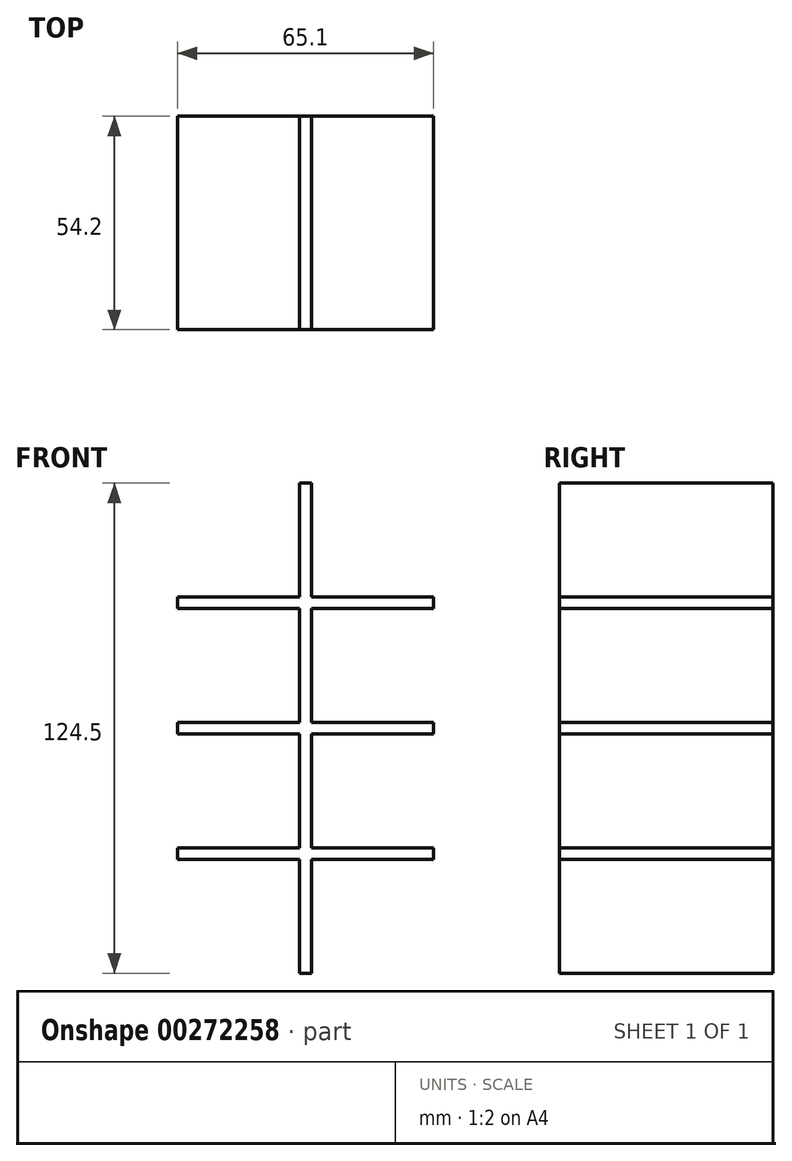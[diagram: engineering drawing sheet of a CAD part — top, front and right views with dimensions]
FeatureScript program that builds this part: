
annotation { "Feature Type Name" : "Feature", "Feature Type Description" : "" }
export const myFeature = defineFeature(function(context is Context, id is Id, definition is map)
    precondition{}
    {
        {
            var Q0;
            Q0=qCreatedBy(makeId("Front.planeOp"),FACE);
            var sketch = newSketch(context, id + "F0", { "sketchPlane" : qUnion([Q0])});
            skLineSegment(sketch, "E0", {"start": v(1.5, 30.37) * mm, "end": v(1.5, 1.5) * mm});
            skLineSegment(sketch, "E1", {"start": v(1.5, 1.5) * mm, "end": v(32.55, 1.5) * mm});
            skLineSegment(sketch, "E2", {"start": v(32.55, 1.5) * mm, "end": v(32.55, -1.5) * mm});
            skLineSegment(sketch, "E3", {"start": v(32.55, -1.5) * mm, "end": v(1.5, -1.5) * mm});
            skLineSegment(sketch, "E4", {"start": v(1.5, -1.5) * mm, "end": v(1.5, -30.38) * mm});
            skLineSegment(sketch, "E5", {"start": v(1.5, -30.37) * mm, "end": v(32.55, -30.37) * mm});
            skLineSegment(sketch, "E6", {"start": v(32.55, -30.38) * mm, "end": v(32.55, -33.37) * mm});
            skLineSegment(sketch, "E7", {"start": v(32.55, -33.37) * mm, "end": v(1.5, -33.37) * mm});
            skLineSegment(sketch, "E8", {"start": v(1.5, -33.37) * mm, "end": v(1.5, -62.25) * mm});
            skLineSegment(sketch, "E9", {"start": v(1.5, -62.25) * mm, "end": v(-1.5, -62.25) * mm});
            skLineSegment(sketch, "E10", {"start": v(-1.5, -62.25) * mm, "end": v(-1.5, -33.37) * mm});
            skLineSegment(sketch, "E11", {"start": v(-1.5, -33.37) * mm, "end": v(-32.55, -33.37) * mm});
            skLineSegment(sketch, "E12", {"start": v(-32.55, -33.37) * mm, "end": v(-32.55, -30.37) * mm});
            skLineSegment(sketch, "E13", {"start": v(-32.55, -30.38) * mm, "end": v(-1.5, -30.37) * mm});
            skLineSegment(sketch, "E14", {"start": v(-1.5, -30.37) * mm, "end": v(-1.5, -1.5) * mm});
            skLineSegment(sketch, "E15", {"start": v(-1.5, -1.5) * mm, "end": v(-32.55, -1.5) * mm});
            skLineSegment(sketch, "E16", {"start": v(-32.55, -1.5) * mm, "end": v(-32.55, 1.5) * mm});
            skLineSegment(sketch, "E17", {"start": v(-32.55, 1.5) * mm, "end": v(-1.5, 1.5) * mm});
            skLineSegment(sketch, "E18", {"start": v(-1.5, 1.5) * mm, "end": v(-1.5, 30.37) * mm});
            skLineSegment(sketch, "E19", {"start": v(-1.5, 30.37) * mm, "end": v(-32.55, 30.37) * mm});
            skLineSegment(sketch, "E20", {"start": v(-32.55, 30.37) * mm, "end": v(-32.55, 33.37) * mm});
            skLineSegment(sketch, "E21", {"start": v(-32.55, 33.37) * mm, "end": v(-1.5, 33.37) * mm});
            skLineSegment(sketch, "E22", {"start": v(-1.5, 62.25) * mm, "end": v(-1.5, 33.37) * mm});
            skLineSegment(sketch, "E23", {"start": v(-1.5, 62.25) * mm, "end": v(1.5, 62.25) * mm});
            skLineSegment(sketch, "E24", {"start": v(1.5, 62.25) * mm, "end": v(1.5, 33.37) * mm});
            skLineSegment(sketch, "E25", {"start": v(1.5, 33.37) * mm, "end": v(32.55, 33.37) * mm});
            skLineSegment(sketch, "E26", {"start": v(32.55, 33.37) * mm, "end": v(32.55, 30.37) * mm});
            skLineSegment(sketch, "E27", {"start": v(32.55, 30.37) * mm, "end": v(1.5, 30.37) * mm});
            skSolve(sketch);
        }
        {
            var Q0;
            Q0 = qSketchRegion(id + "F0", true);
            extrude(context, id + "F1", {"entities" : qUnion([Q0]), "depth" : 54.2 * mm});
        }
    });
